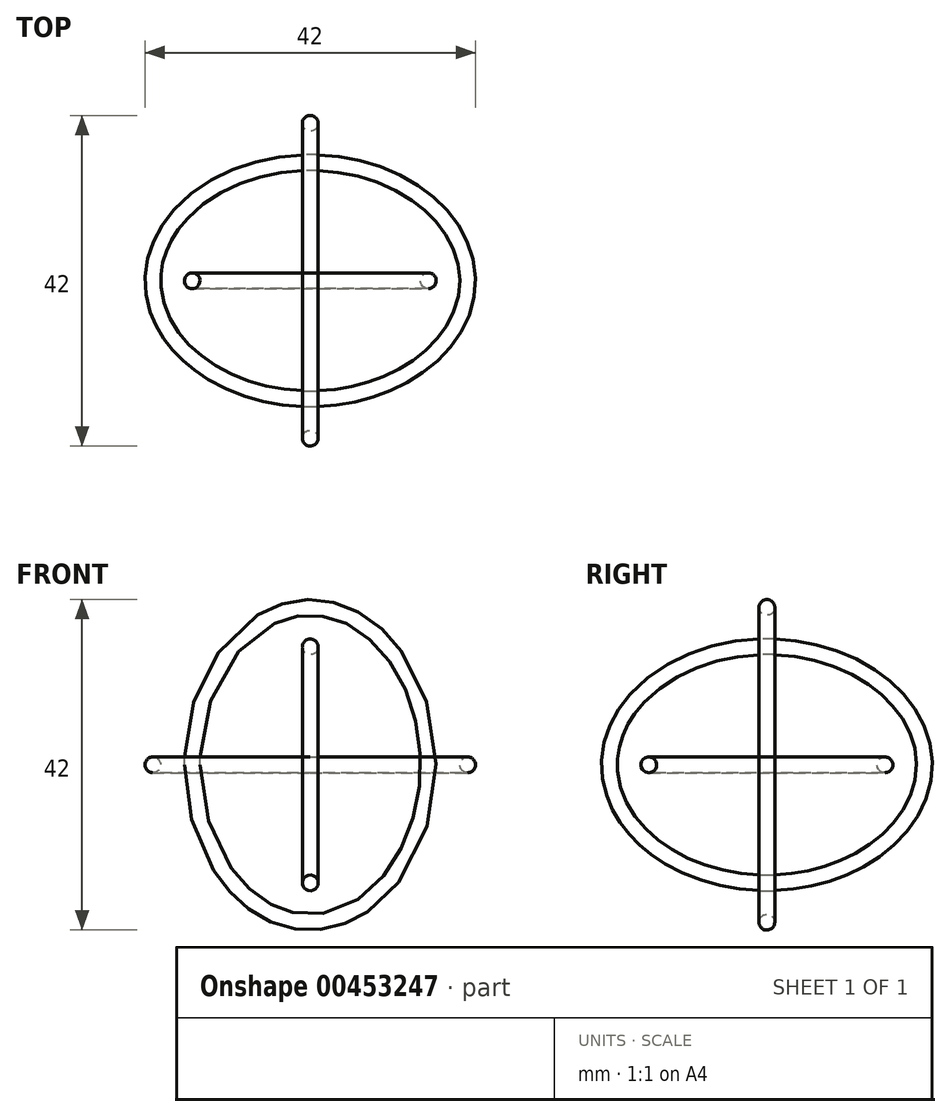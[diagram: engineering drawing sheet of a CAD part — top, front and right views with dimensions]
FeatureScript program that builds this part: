
annotation { "Feature Type Name" : "Feature", "Feature Type Description" : "" }
export const myFeature = defineFeature(function(context is Context, id is Id, definition is map)
    precondition{}
    {
        {
            var Q0;
            Q0=qCreatedBy(makeId("Top.planeOp"),FACE);
            var sketch = newSketch(context, id + "F0", { "sketchPlane" : qUnion([Q0])});
            skEllipse(sketch, "E0", {"center": v(0, 0) * mm, "majorRadius": 25 * mm, "minorRadius": 20 * mm, "majorAxis": v(-1, 0)});
            skPoint(sketch, "E1", {"position": v(0, -15) * mm});
            skLineSegment(sketch, "E2", {"start": v(0, 0) * mm, "end": v(18.1, 0) * mm, "construction": true});
            skLineSegment(sketch, "E3", {"start": v(0, 0) * mm, "end": v(0, 13.78) * mm, "construction": true});
            skSolve(sketch);
        }
        {
            var Q0;
            Q0=qCreatedBy(makeId("Right.planeOp"),FACE);
            var sketch = newSketch(context, id + "F1", { "sketchPlane" : qUnion([Q0])});
            skPoint(sketch, "E4.0", {"position": v(-15, 0) * mm});
            skCircle(sketch, "E5", {"center": v(-15, 0) * mm, "radius": 1 * mm});
            skLineSegment(sketch, "E6", {"start": v(0, 0) * mm, "end": v(0, 18.74) * mm, "construction": true});
            skSolve(sketch);
        }
        {
            var Q0;
            Q0=makeQuery(id+"F1.imprint","IMPRINT",FACE,{"disambiguationData":[TD([[makeQuery(id+"F1.imprint","IMPRINT",EDGE,{"derivedFrom":sQuery(id+"F1.wireOp",EDGE,"E5")}),1.0]])]});
            var Q1;
            Q1=sQuery(id+"F0.wireOp",EDGE,"E0");
            sweep(context, id + "F2", {"profiles" : qUnion([Q0]), "path" : qUnion([Q1])});
        }
        {
            var Q0;
            Q0=makeQuery(id+"F2.opSweep","SWEPT_BODY",BODY,{"disambiguationData":[OSD([sQuery(id+"F0.wireOp",EDGE,"E0"),sQuery(id+"F1.wireOp",EDGE,"E5")])]});
            var Q1;
            Q1=sQuery(id+"F0.wireOp",EDGE,"E2");
            transform(context, id + "F3", {"entities" : qUnion([Q0]), "transformType" : TransformType.ROTATION, "transformAxis" : qUnion([Q1]), "angle" : 90 * degree, "makeCopy" : true});
        }
        {
            var Q0;
            Q0=makeQuery(id+"F3.opPattern","COPY",BODY,{"derivedFrom":makeQuery(id+"F2.opSweep","SWEPT_BODY",BODY,{"disambiguationData":[OSD([sQuery(id+"F0.wireOp",EDGE,"E0"),sQuery(id+"F1.wireOp",EDGE,"E5")])]}),"instanceName":"1"});
            var Q1;
            Q1=sQuery(id+"F1.wireOp",EDGE,"E6");
            transform(context, id + "F4", {"entities" : qUnion([Q0]), "transformType" : TransformType.ROTATION, "transformAxis" : qUnion([Q1]), "angle" : 90 * degree, "makeCopy" : false});
        }
        {
            var Q0;
            Q0=makeQuery(id+"F3.opPattern","COPY",BODY,{"derivedFrom":makeQuery(id+"F2.opSweep","SWEPT_BODY",BODY,{"disambiguationData":[OSD([sQuery(id+"F0.wireOp",EDGE,"E0"),sQuery(id+"F1.wireOp",EDGE,"E5")])]}),"instanceName":"1"});
            var Q1;
            Q1=sQuery(id+"F1.wireOp",EDGE,"E6");
            transform(context, id + "F5", {"entities" : qUnion([Q0]), "transformType" : TransformType.ROTATION, "transformAxis" : qUnion([Q1]), "angle" : 90 * degree, "makeCopy" : true});
        }
        {
            var Q0;
            Q0=makeQuery(id+"F5.opPattern","COPY",BODY,{"derivedFrom":makeQuery(id+"F3.opPattern","COPY",BODY,{"derivedFrom":makeQuery(id+"F2.opSweep","SWEPT_BODY",BODY,{"disambiguationData":[OSD([sQuery(id+"F0.wireOp",EDGE,"E0"),sQuery(id+"F1.wireOp",EDGE,"E5")])]}),"instanceName":"1"}),"instanceName":"1"});
            var Q1;
            Q1=sQuery(id+"F0.wireOp",EDGE,"E3");
            transform(context, id + "F6", {"entities" : qUnion([Q0]), "transformType" : TransformType.ROTATION, "transformAxis" : qUnion([Q1]), "angle" : 90 * degree, "makeCopy" : false});
        }
    });
